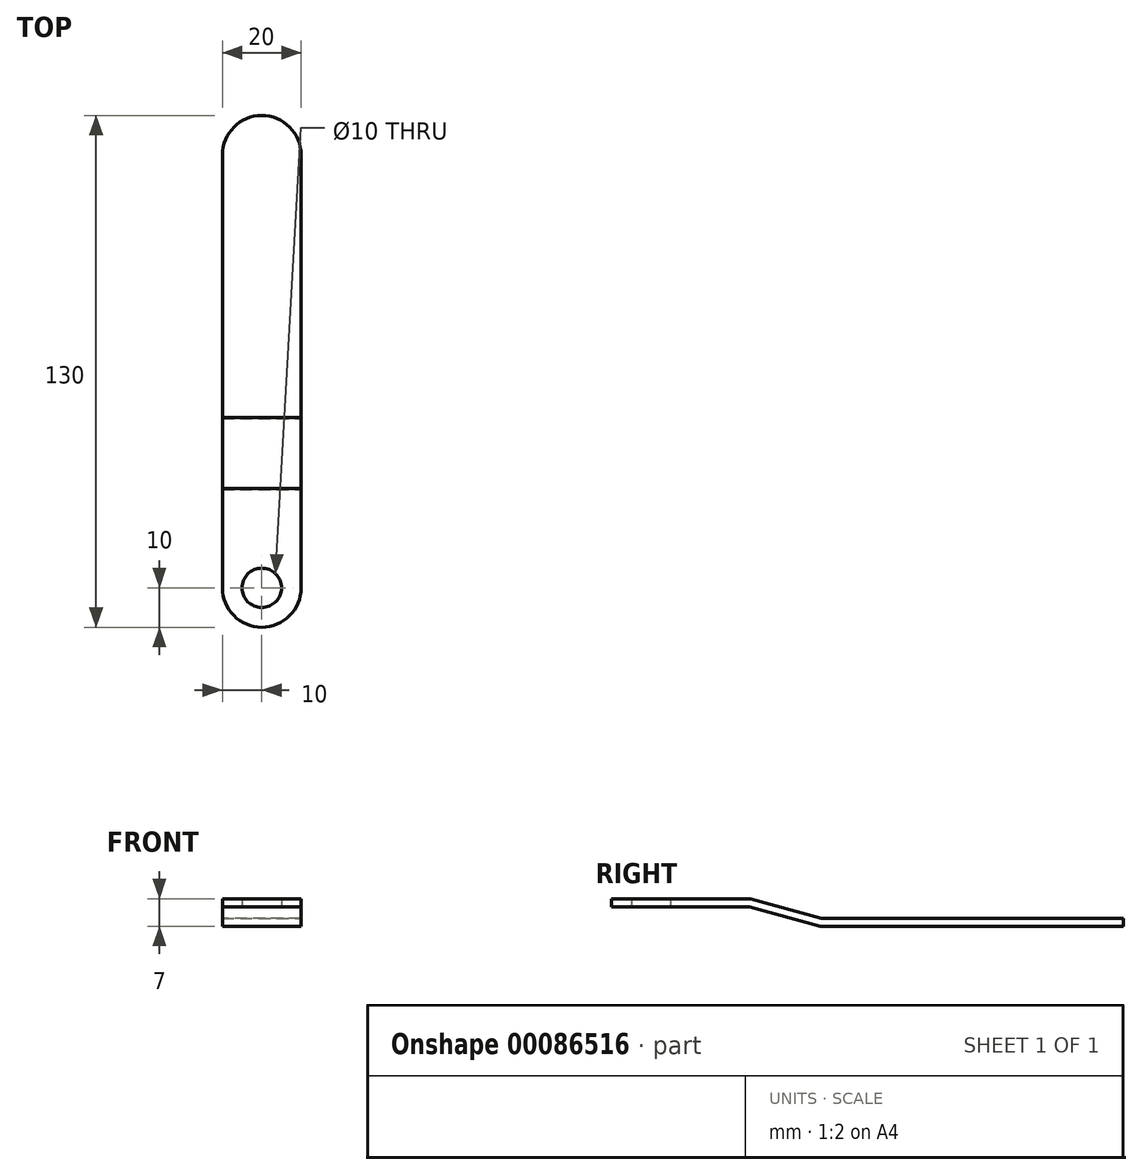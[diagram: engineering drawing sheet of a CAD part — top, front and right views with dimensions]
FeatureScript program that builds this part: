
annotation { "Feature Type Name" : "Feature", "Feature Type Description" : "" }
export const myFeature = defineFeature(function(context is Context, id is Id, definition is map)
    precondition{}
    {
        {
            var Q0;
            Q0=qCreatedBy(makeId("Top.planeOp"),FACE);
            var sketch = newSketch(context, id + "F0", { "sketchPlane" : qUnion([Q0])});
            skCircle(sketch, "E0", {"center": v(0, 0) * mm, "radius": 5 * mm});
            skArc(sketch, "E1", {"start": v(-10, 0) * mm, "mid": v(0, -10) * mm, "end": v(10, 0) * mm});
            skLineSegment(sketch, "E2", {"start": v(-10, 0) * mm, "end": v(-10, 110) * mm});
            skLineSegment(sketch, "E3", {"start": v(10, 110) * mm, "end": v(10, 0) * mm});
            skArc(sketch, "E4", {"start": v(-10, 110) * mm, "mid": v(0, 120) * mm, "end": v(10, 110) * mm});
            skSolve(sketch);
        }
        {
            var Q0;
            Q0=makeQuery(id+"F0.imprint","IMPRINT",FACE,{"disambiguationData":[TD([[makeQuery(id+"F0.imprint","IMPRINT",EDGE,{"derivedFrom":sQuery(id+"F0.wireOp",EDGE,"E0")}),-1.0]])]});
            extrude(context, id + "F1", {"entities" : qUnion([Q0]), "depth" : 7 * mm});
        }
        {
            var Q0;
            Q0=qCreatedBy(makeId("Right.planeOp"),FACE);
            var sketch = newSketch(context, id + "F2", { "sketchPlane" : qUnion([Q0])});
            skLineSegment(sketch, "E5", {"start": v(-10, 5) * mm, "end": v(25, 5) * mm});
            skLineSegment(sketch, "E6", {"start": v(25, 5) * mm, "end": v(43, 0) * mm});
            skLineSegment(sketch, "E7", {"start": v(43, 0) * mm, "end": v(120, 0) * mm});
            skLineSegment(sketch, "E8", {"start": v(120, 0) * mm, "end": v(120, 2) * mm});
            skLineSegment(sketch, "E9", {"start": v(120, 2) * mm, "end": v(43.27, 2) * mm});
            skLineSegment(sketch, "E10", {"start": v(43.27, 2) * mm, "end": v(25.27, 7) * mm});
            skLineSegment(sketch, "E11", {"start": v(25.27, 7) * mm, "end": v(-10, 7) * mm});
            skLineSegment(sketch, "E12", {"start": v(-10, 7) * mm, "end": v(-10, 5) * mm});
            skSolve(sketch);
        }
        {
            var Q0;
            Q0 = qSketchRegion(id + "F2", true);
            extrude(context, id + "F3", {"entities" : qUnion([Q0]), "operationType" : NewBodyOperationType.INTERSECT, "endBound" : BoundingType.SYMMETRIC, "oppositeDirection" : true, "depth" : 20 * mm});
        }
    });
